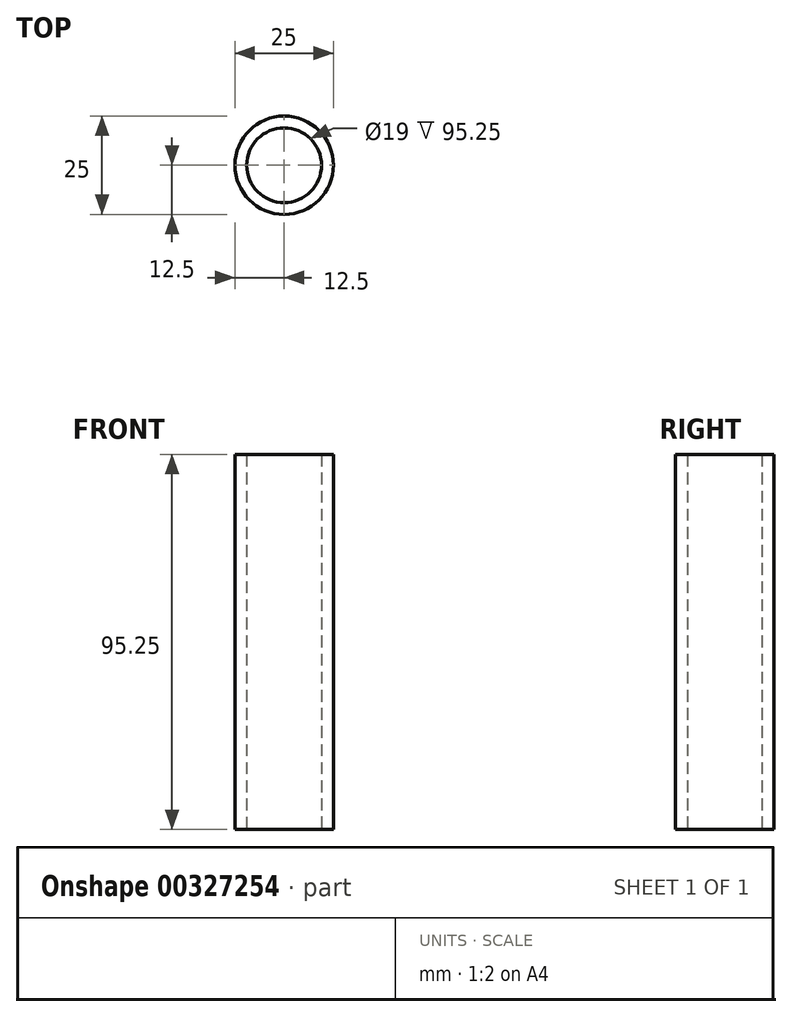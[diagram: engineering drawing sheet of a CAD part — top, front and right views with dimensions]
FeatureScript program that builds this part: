
annotation { "Feature Type Name" : "Feature", "Feature Type Description" : "" }
export const myFeature = defineFeature(function(context is Context, id is Id, definition is map)
    precondition{}
    {
        {
            var Q0;
            Q0=qCreatedBy(makeId("Top.planeOp"),FACE);
            var sketch = newSketch(context, id + "F0", { "sketchPlane" : qUnion([Q0])});
            skCircle(sketch, "E0", {"center": v(0, 0) * mm, "radius": 12.5 * mm});
            skSolve(sketch);
        }
        {
            var Q0;
            Q0 = qSketchRegion(id + "F0", true);
            extrude(context, id + "F1", {"entities" : qUnion([Q0]), "depth" : 95.25 * mm, "offsetDistance" : 25 * mm});
        }
        {
            var Q0;
            Q0=makeQuery(id+"F1.opExtrude","CAP_FACE",FACE,{"disambiguationData":[OSD([sQuery(id+"F0.wireOp",EDGE,"E0")])],"isStart":true});
            var sketch = newSketch(context, id + "F2", { "sketchPlane" : qUnion([Q0])});
            skCircle(sketch, "E1", {"center": v(0, 0) * mm, "radius": 9.5 * mm});
            skSolve(sketch);
        }
        {
            var Q0;
            Q0 = qSketchRegion(id + "F2", true);
            extrude(context, id + "F3", {"entities" : qUnion([Q0]), "operationType" : NewBodyOperationType.REMOVE, "endBound" : BoundingType.THROUGH_ALL, "oppositeDirection" : true, "depth" : 25 * mm});
        }
    });
